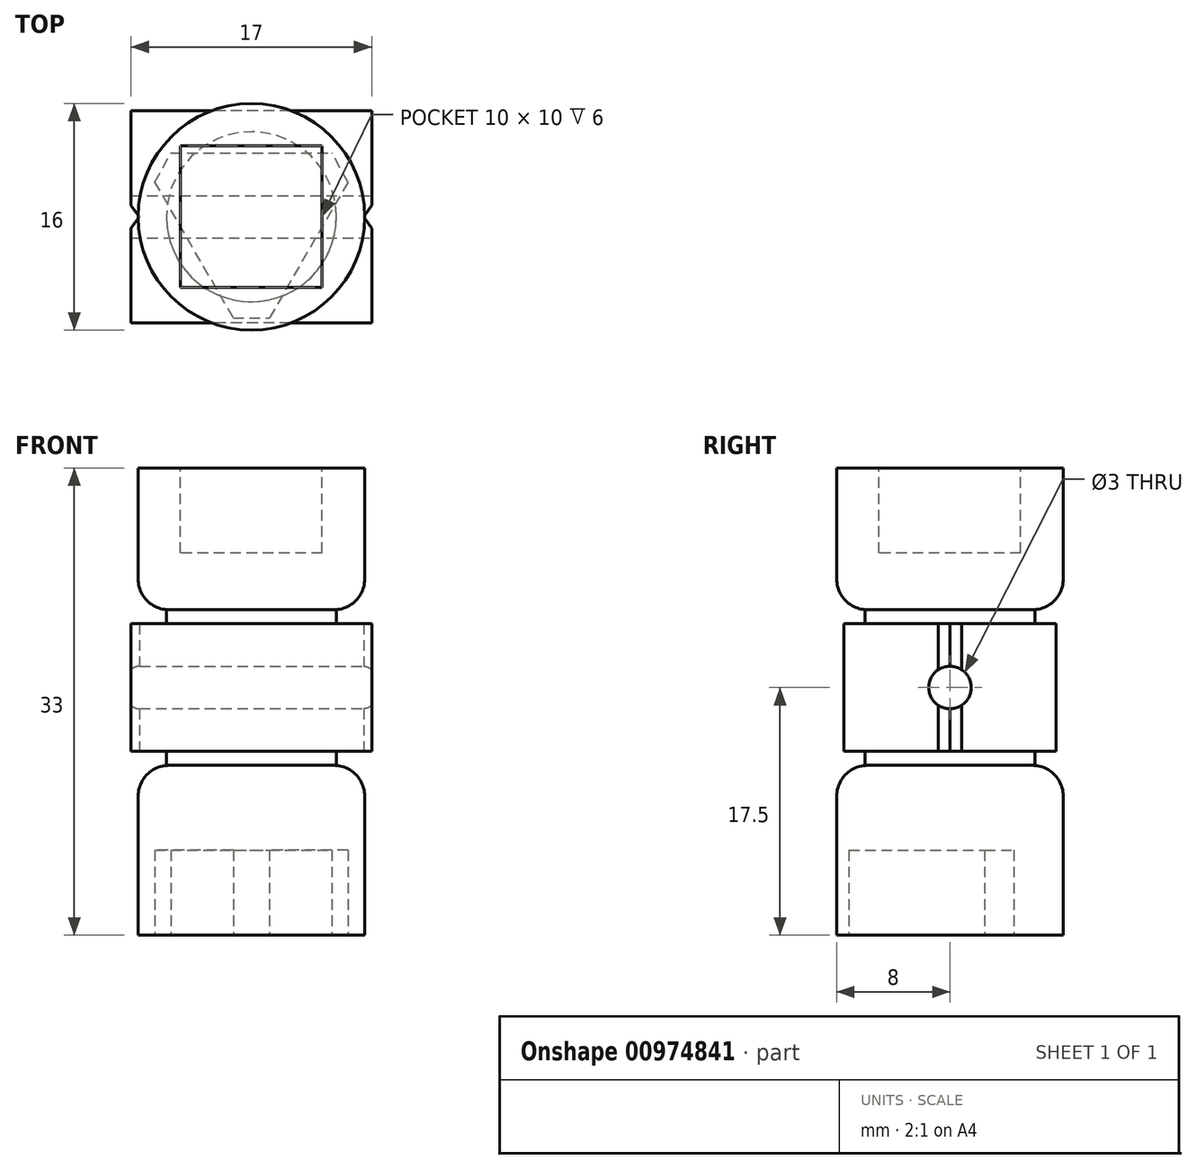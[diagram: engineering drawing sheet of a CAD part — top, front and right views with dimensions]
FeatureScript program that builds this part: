
annotation { "Feature Type Name" : "Feature", "Feature Type Description" : "" }
export const myFeature = defineFeature(function(context is Context, id is Id, definition is map)
    precondition{}
    {
        {
            var Q0;
            Q0=qCreatedBy(makeId("Top.planeOp"),FACE);
            var sketch = newSketch(context, id + "F0", { "sketchPlane" : qUnion([Q0])});
            skLineSegment(sketch, "E0.bottom", {"start": v(8.5, 7.5) * mm, "end": v(-8.5, 7.5) * mm});
            skLineSegment(sketch, "E0.top", {"start": v(8.5, -7.5) * mm, "end": v(-8.5, -7.5) * mm});
            skLineSegment(sketch, "E0.left", {"start": v(8.5, 7.5) * mm, "end": v(8.5, -7.5) * mm});
            skLineSegment(sketch, "E0.right", {"start": v(-8.5, 7.5) * mm, "end": v(-8.5, -7.5) * mm});
            skSolve(sketch);
        }
        {
            var Q0;
            Q0=qSketchRegion(id+"F0",true);
            extrude(context, id + "F1", {"entities" : qUnion([Q0]), "endBound" : BoundingType.SYMMETRIC, "depth" : 9 * mm, "offsetDistance" : 25 * mm});
        }
        {
            var Q0;
            Q0=makeQuery(id+"F1.opExtrude","CAP_FACE",FACE,{"disambiguationData":[OSD([sQuery(id+"F0.wireOp",EDGE,"E0.bottom"),sQuery(id+"F0.wireOp",EDGE,"E0.top"),sQuery(id+"F0.wireOp",EDGE,"E0.left"),sQuery(id+"F0.wireOp",EDGE,"E0.right")])],"isStart":false});
            var sketch = newSketch(context, id + "F2", { "sketchPlane" : qUnion([Q0])});
            skCircle(sketch, "E1", {"center": v(0, 0) * mm, "radius": 6 * mm});
            skSolve(sketch);
        }
        {
            var Q0;
            Q0=qSketchRegion(id+"F2",true);
            extrude(context, id + "F3", {"entities" : qUnion([Q0]), "depth" : 1 * mm, "offsetDistance" : 25 * mm});
        }
        {
            var Q0;
            Q0=makeQuery(id+"F1.opExtrude","CAP_FACE",FACE,{"disambiguationData":[OSD([sQuery(id+"F0.wireOp",EDGE,"E0.bottom"),sQuery(id+"F0.wireOp",EDGE,"E0.top"),sQuery(id+"F0.wireOp",EDGE,"E0.left"),sQuery(id+"F0.wireOp",EDGE,"E0.right")])],"isStart":true});
            var sketch = newSketch(context, id + "F4", { "sketchPlane" : qUnion([Q0])});
            skCircle(sketch, "E2", {"center": v(0, 0) * mm, "radius": 6 * mm});
            skSolve(sketch);
        }
        {
            var Q0;
            Q0=qSketchRegion(id+"F4",true);
            extrude(context, id + "F5", {"entities" : qUnion([Q0]), "depth" : 1 * mm, "offsetDistance" : 25 * mm});
        }
        {
            var Q0;
            Q0=makeQuery(id+"F1.opExtrude","SWEPT_FACE",FACE,{"disambiguationData":[OSD([sQuery(id+"F0.wireOp",EDGE,"E0.left")])]});
            var sketch = newSketch(context, id + "F6", { "sketchPlane" : qUnion([Q0])});
            skCircle(sketch, "E3", {"center": v(0, 0) * mm, "radius": 1.5 * mm});
            skSolve(sketch);
        }
        {
            var Q0;
            Q0=qSketchRegion(id+"F6",true);
            extrude(context, id + "F7", {"entities" : qUnion([Q0]), "operationType" : NewBodyOperationType.REMOVE, "endBound" : BoundingType.THROUGH_ALL, "oppositeDirection" : true, "depth" : 25 * mm, "offsetDistance" : 25 * mm});
        }
        {
            var Q0;
            Q0=makeQuery(id+"F1.opExtrude","CAP_FACE",FACE,{"disambiguationData":[OSD([sQuery(id+"F0.wireOp",EDGE,"E0.bottom"),sQuery(id+"F0.wireOp",EDGE,"E0.top"),sQuery(id+"F0.wireOp",EDGE,"E0.left"),sQuery(id+"F0.wireOp",EDGE,"E0.right")])],"isStart":true});
            var sketch = newSketch(context, id + "F8", { "sketchPlane" : qUnion([Q0])});
            skLineSegment(sketch, "E4", {"start": v(7.94, 0) * mm, "end": v(8.5, 0.83) * mm});
            skLineSegment(sketch, "E5", {"start": v(7.94, 0) * mm, "end": v(8.5, -0.83) * mm});
            skLineSegment(sketch, "E6", {"start": v(8.5, 0.83) * mm, "end": v(8.5, -0.83) * mm});
            skLineSegment(sketch, "E7", {"start": v(-7.9, 0) * mm, "end": v(-8.5, 0.8) * mm});
            skLineSegment(sketch, "E8", {"start": v(-7.9, 0) * mm, "end": v(-8.5, -0.8) * mm});
            skLineSegment(sketch, "E9", {"start": v(-8.5, -0.8) * mm, "end": v(-8.5, 0.8) * mm});
            skSolve(sketch);
        }
        {
            var Q0;
            Q0=qSketchRegion(id+"F8",true);
            extrude(context, id + "F9", {"entities" : qUnion([Q0]), "operationType" : NewBodyOperationType.REMOVE, "endBound" : BoundingType.THROUGH_ALL, "oppositeDirection" : true, "depth" : 25 * mm, "offsetDistance" : 25 * mm});
        }
        {
            var Q0;
            Q0=makeQuery(id+"F3.opExtrude","CAP_FACE",FACE,{"disambiguationData":[OSD([sQuery(id+"F2.wireOp",EDGE,"E1")])],"isStart":false});
            var sketch = newSketch(context, id + "F10", { "sketchPlane" : qUnion([Q0])});
            skCircle(sketch, "E10", {"center": v(0, 0) * mm, "radius": 8 * mm});
            skSolve(sketch);
        }
        {
            var Q0;
            Q0=qSketchRegion(id+"F10",true);
            extrude(context, id + "F11", {"entities" : qUnion([Q0]), "operationType" : NewBodyOperationType.ADD, "depth" : 10 * mm, "offsetDistance" : 25 * mm});
        }
        {
            var Q0;
            Q0=makeQuery(id+"F5.opExtrude","CAP_FACE",FACE,{"disambiguationData":[OSD([sQuery(id+"F4.wireOp",EDGE,"E2")])],"isStart":false});
            var sketch = newSketch(context, id + "F12", { "sketchPlane" : qUnion([Q0])});
            skCircle(sketch, "E11", {"center": v(0, 0) * mm, "radius": 8 * mm});
            skSolve(sketch);
        }
        {
            var Q0;
            Q0=makeQuery(id+"F12.imprint","IMPRINT",FACE,{"disambiguationData":[TD([[makeQuery(id+"F12.imprint","IMPRINT",EDGE,{"derivedFrom":sQuery(id+"F12.wireOp",EDGE,"E11")}),1.0]])]});
            var Q1;
            Q1=makeQuery(id+"F12.imprint","IMPRINT",FACE,{"disambiguationData":[TD([[makeQuery(id+"F12.imprint","IMPRINT",EDGE,{"derivedFrom":makeQuery(id+"F5.opExtrude","CAP_EDGE",EDGE,{"disambiguationData":[OSD([sQuery(id+"F4.wireOp",EDGE,"E2")])],"isStart":false})}),1.0]])]});
            extrude(context, id + "F13", {"entities" : qUnion([Q0, Q1]), "depth" : 12 * mm, "offsetDistance" : 25 * mm});
        }
        {
            var Q0;
            Q0=makeQuery(id+"F11.opExtrude","CAP_EDGE",EDGE,{"disambiguationData":[OSD([sQuery(id+"F10.wireOp",EDGE,"E10")])],"isStart":true});
            var Q1;
            Q1=makeQuery(id+"F13.opExtrude","CAP_EDGE",EDGE,{"disambiguationData":[OSD([sQuery(id+"F12.wireOp",EDGE,"E11")])],"isStart":true});
            fillet(context, id + "F14", {"entities" : qUnion([Q0, Q1]), "radius" : 2.17 * mm, "tangentPropagation" : true, "allowEdgeOverflow" : false});
        }
        {
            var Q0;
            Q0=makeQuery(id+"F13.opExtrude","CAP_FACE",FACE,{"disambiguationData":[OSD([sQuery(id+"F12.wireOp",EDGE,"E11")])],"isStart":false});
            var sketch = newSketch(context, id + "F15", { "sketchPlane" : qUnion([Q0])});
            skLineSegment(sketch, "E12", {"start": v(-1.28, 7.14) * mm, "end": v(-6.82, -2.46) * mm});
            skLineSegment(sketch, "E13", {"start": v(-5.68, -4.5) * mm, "end": v(5.68, -4.5) * mm});
            skLineSegment(sketch, "E14", {"start": v(6.82, -2.46) * mm, "end": v(1.28, 7.14) * mm});
            skPoint(sketch, "E15.orphan", {"position": v(0, 9.36) * mm});
            skPoint(sketch, "E16.center.orphan", {"position": v(0, 0) * mm});
            skLineSegment(sketch, "E17", {"start": v(-1.28, 7.14) * mm, "end": v(1.28, 7.14) * mm});
            skLineSegment(sketch, "E18", {"start": v(-6.82, -2.46) * mm, "end": v(-5.68, -4.5) * mm});
            skLineSegment(sketch, "E19", {"start": v(6.82, -2.46) * mm, "end": v(5.68, -4.5) * mm});
            skSolve(sketch);
        }
        {
            var Q0;
            Q0=qSketchRegion(id+"F15",true);
            extrude(context, id + "F16", {"entities" : qUnion([Q0]), "operationType" : NewBodyOperationType.REMOVE, "oppositeDirection" : true, "depth" : 6 * mm, "offsetDistance" : 25 * mm});
        }
        {
            var Q0;
            Q0=makeQuery(id+"F11.opExtrude","CAP_FACE",FACE,{"disambiguationData":[OSD([sQuery(id+"F10.wireOp",EDGE,"E10")])],"isStart":false});
            var sketch = newSketch(context, id + "F17", { "sketchPlane" : qUnion([Q0])});
            skLineSegment(sketch, "E20.bottom", {"start": v(5, 5) * mm, "end": v(-5, 5) * mm});
            skLineSegment(sketch, "E20.top", {"start": v(5, -5) * mm, "end": v(-5, -5) * mm});
            skLineSegment(sketch, "E20.left", {"start": v(5, 5) * mm, "end": v(5, -5) * mm});
            skLineSegment(sketch, "E20.right", {"start": v(-5, 5) * mm, "end": v(-5, -5) * mm});
            skSolve(sketch);
        }
        {
            var Q0;
            Q0=qSketchRegion(id+"F17",true);
            extrude(context, id + "F18", {"entities" : qUnion([Q0]), "operationType" : NewBodyOperationType.REMOVE, "oppositeDirection" : true, "depth" : 6 * mm, "offsetDistance" : 25 * mm});
        }
    });
